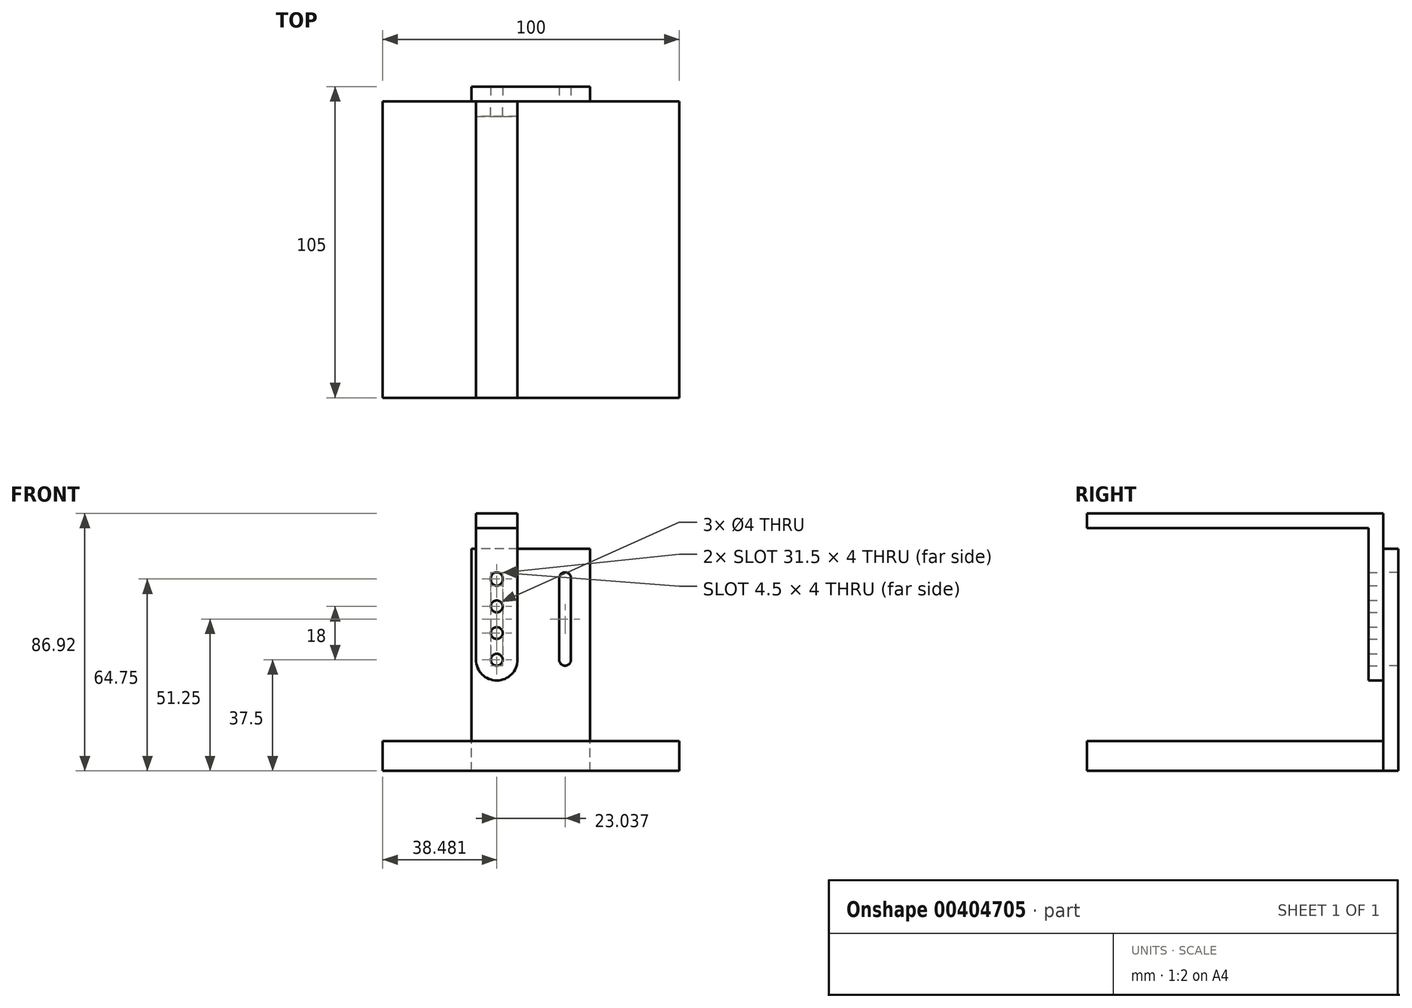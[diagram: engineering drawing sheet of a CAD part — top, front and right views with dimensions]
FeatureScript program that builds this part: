
annotation { "Feature Type Name" : "Feature", "Feature Type Description" : "" }
export const myFeature = defineFeature(function(context is Context, id is Id, definition is map)
    precondition{}
    {
        {
            assignVariable(context, id + "F0", {"name" : "zSizeBase", "anyValue" : 10});
        }
        {
            assignVariable(context, id + "F1", {"name" : "ySizeArm", "anyValue" : 5});
        }
        {
            assignVariable(context, id + "F2", {"name" : "zSizeTop", "anyValue" : 5});
        }
        {
            var Q0;
            Q0=qCreatedBy(makeId("Top.planeOp"),FACE);
            var sketch = newSketch(context, id + "F3", { "sketchPlane" : qUnion([Q0])});
            skLineSegment(sketch, "E0.bottom", {"start": v(50, -50) * mm, "end": v(-50, -50) * mm});
            skLineSegment(sketch, "E0.top", {"start": v(50, 50) * mm, "end": v(-50, 50) * mm});
            skLineSegment(sketch, "E0.left", {"start": v(50, -50) * mm, "end": v(50, 50) * mm});
            skLineSegment(sketch, "E0.right", {"start": v(-50, -50) * mm, "end": v(-50, 50) * mm});
            skPoint(sketch, "E0.middle", {"position": v(0, 0) * mm});
            skSolve(sketch);
        }
        {
            var Q0;
            Q0=makeQuery(id+"F3.imprint","IMPRINT",FACE,{"disambiguationData":[TD([[makeQuery(id+"F3.imprint","IMPRINT",EDGE,{"derivedFrom":sQuery(id+"F3.wireOp",EDGE,"E0.bottom")}),-1.0]])]});
            extrude(context, id + "F4", {"entities" : qUnion([Q0]), "depth" : (getVariable(context, 'zSizeBase')) * mm});
        }
        {
            var Q0;
            Q0=makeQuery(id+"F4.opExtrude","SWEPT_FACE",FACE,{"disambiguationData":[OSD([sQuery(id+"F3.wireOp",EDGE,"E0.top")])]});
            var sketch = newSketch(context, id + "F5", { "sketchPlane" : qUnion([Q0])});
            skLineSegment(sketch, "E1.bottom", {"start": v(-20, 0) * mm, "end": v(20, 0) * mm});
            skLineSegment(sketch, "E1.top", {"start": v(-20, 75) * mm, "end": v(20, 75) * mm});
            skLineSegment(sketch, "E1.left", {"start": v(-20, 0) * mm, "end": v(-20, 75) * mm});
            skLineSegment(sketch, "E1.right", {"start": v(20, 0) * mm, "end": v(20, 75) * mm});
            skLineSegment(sketch, "E2", {"start": v(0, 37.5) * mm, "end": v(0, 75) * mm, "construction": true});
            skLineSegment(sketch, "E3", {"start": v(0, 37.5) * mm, "end": v(0, 0) * mm, "construction": true});
            skLineSegment(sketch, "E4", {"start": v(-11.52, 75) * mm, "end": v(-11.52, 37.5) * mm, "construction": true});
            skPoint(sketch, "E4.startSnap0", {"position": v(-11.52, 37.5) * mm});
            skPoint(sketch, "E5.startSnap0", {"position": v(10, 37.5) * mm});
            skArc(sketch, "E6", {"start": v(-13.52, 65) * mm, "mid": v(-11.52, 67) * mm, "end": v(-9.52, 65) * mm});
            skLineSegment(sketch, "E7", {"start": v(-13.52, 65) * mm, "end": v(-13.52, 37.5) * mm});
            skLineSegment(sketch, "E8", {"start": v(-9.52, 65) * mm, "end": v(-9.52, 37.5) * mm});
            skArc(sketch, "E9", {"start": v(-13.52, 37.5) * mm, "mid": v(-11.52, 35.5) * mm, "end": v(-9.52, 37.5) * mm});
            skLineSegment(sketch, "E10.MirrorCS", {"start": v(9.52, 65) * mm, "end": v(9.52, 37.5) * mm});
            skArc(sketch, "E11.MirrorCS", {"start": v(13.52, 37.5) * mm, "mid": v(11.52, 35.5) * mm, "end": v(9.52, 37.5) * mm});
            skLineSegment(sketch, "E12.MirrorCS", {"start": v(13.52, 65) * mm, "end": v(13.52, 37.5) * mm});
            skArc(sketch, "E13.MirrorCS", {"start": v(13.52, 65) * mm, "mid": v(11.52, 67) * mm, "end": v(9.52, 65) * mm});
            skSolve(sketch);
        }
        {
            var Q0;
            {var subQ0=sQuery(id+"F5.wireOp",EDGE,"E1.top");Q0=makeQuery(id+"F5.imprint","IMPRINT",FACE,{"disambiguationData":[TD([[makeQuery(id+"F5.imprint","IMPRINT",EDGE,{"derivedFrom":subQ0}),-1.0]])]});}
            var Q1;
            {var subQ0=sQuery(id+"F5.wireOp",EDGE,"E1.bottom");Q1=makeQuery(id+"F5.imprint","IMPRINT",FACE,{"disambiguationData":[TD([[makeQuery(id+"F5.imprint","IMPRINT",EDGE,{"derivedFrom":subQ0}),1.0]])]});}
            extrude(context, id + "F6", {"entities" : qUnion([Q0, Q1]), "operationType" : NewBodyOperationType.ADD, "depth" : (getVariable(context, 'ySizeArm')) * mm});
        }
        {
            var Q0;
            {var subQ0=sQuery(id+"F5.wireOp",EDGE,"E1.top");Q0=makeQuery(id+"F5.imprint","IMPRINT",FACE,{"disambiguationData":[TD([[makeQuery(id+"F5.imprint","IMPRINT",EDGE,{"derivedFrom":subQ0}),-1.0]])]});}
            var sketch = newSketch(context, id + "F7", { "sketchPlane" : qUnion([Q0])});
            skPoint(sketch, "E14.0", {"position": v(11.52, 37.5) * mm});
            skPoint(sketch, "E15.0", {"position": v(9.52, 37.5) * mm});
            skArc(sketch, "E16", {"start": v(4.52, 37.5) * mm, "mid": v(11.52, 30.5) * mm, "end": v(18.52, 37.5) * mm});
            skPoint(sketch, "E17.0", {"position": v(0, 75) * mm});
            skLineSegment(sketch, "E18", {"start": v(4.52, 37.5) * mm, "end": v(4.52, 81.92) * mm});
            skLineSegment(sketch, "E19", {"start": v(4.52, 81.92) * mm, "end": v(18.52, 81.92) * mm});
            skLineSegment(sketch, "E20", {"start": v(18.52, 81.92) * mm, "end": v(18.52, 37.5) * mm});
            skLineSegment(sketch, "E21", {"start": v(18.52, 37.5) * mm, "end": v(11.52, 37.5) * mm, "construction": true});
            skLineSegment(sketch, "E22", {"start": v(11.52, 37.5) * mm, "end": v(4.52, 37.5) * mm, "construction": true});
            skLineSegment(sketch, "E23", {"start": v(18.52, 81.92) * mm, "end": v(18.52, 86.92) * mm});
            skLineSegment(sketch, "E24", {"start": v(18.52, 86.92) * mm, "end": v(4.52, 86.92) * mm});
            skLineSegment(sketch, "E25", {"start": v(4.52, 86.92) * mm, "end": v(4.52, 81.92) * mm});
            skPoint(sketch, "E26.0", {"position": v(11.52, 65) * mm});
            skCircle(sketch, "E27", {"center": v(11.52, 37.5) * mm, "radius": 2 * mm});
            skCircle(sketch, "E28.0.1.0", {"center": v(11.52, 46.5) * mm, "radius": 2 * mm});
            skCircle(sketch, "E28.0.2.0", {"center": v(11.52, 55.5) * mm, "radius": 2 * mm});
            skCircle(sketch, "E28.0.3.0", {"center": v(11.52, 64.5) * mm, "radius": 2 * mm});
            skLineSegment(sketch, "E28.direction1", {"start": v(11.52, 37.5) * mm, "end": v(36.52, 37.5) * mm, "construction": true});
            skLineSegment(sketch, "E28.direction2", {"start": v(11.52, 37.5) * mm, "end": v(11.52, 46.5) * mm, "construction": true});
            skSolve(sketch);
        }
        {
            var Q0;
            Q0=makeQuery(id+"F7.imprint","IMPRINT",FACE,{"disambiguationData":[TD([[makeQuery(id+"F7.imprint","IMPRINT",EDGE,{"derivedFrom":sQuery(id+"F7.wireOp",EDGE,"E19")}),1.0]])]});
            var Q1;
            {var subQ0=sQuery(id+"F7.wireOp",EDGE,"E19");Q1=makeQuery(id+"F7.imprint","IMPRINT",FACE,{"disambiguationData":[TD([[makeQuery(id+"F7.imprint","IMPRINT",EDGE,{"derivedFrom":subQ0}),-1.0]])]});}
            var Q2;
            {var subQ0=sQuery(id+"F7.wireOp",EDGE,"E28.0.1.0");var subQ1=makeQuery(id+"F5.imprint","IMPRINT",EDGE,{"derivedFrom":sQuery(id+"F5.wireOp",EDGE,"E10.MirrorCS")});var subQ2=makeQuery(id+"F7.imprint","INTERSECT",VERTEX,{"derivedFrom":[subQ1,subQ0]});Q2=makeQuery(id+"F7.imprint","IMPRINT",FACE,{"disambiguationData":[TD([[makeQuery(id+"F7.imprint","IMPRINT",EDGE,{"disambiguationData":[TD([[subQ2,1.0]])],"derivedFrom":subQ0}),-1.0]])]});}
            var Q3;
            {var subQ0=sQuery(id+"F7.wireOp",EDGE,"E28.0.2.0");var subQ1=makeQuery(id+"F5.imprint","IMPRINT",EDGE,{"derivedFrom":sQuery(id+"F5.wireOp",EDGE,"E10.MirrorCS")});var subQ2=makeQuery(id+"F7.imprint","INTERSECT",VERTEX,{"derivedFrom":[subQ1,subQ0]});Q3=makeQuery(id+"F7.imprint","IMPRINT",FACE,{"disambiguationData":[TD([[makeQuery(id+"F7.imprint","IMPRINT",EDGE,{"disambiguationData":[TD([[subQ2,1.0]])],"derivedFrom":subQ0}),-1.0]])]});}
            var Q4;
            {var subQ0=sQuery(id+"F7.wireOp",EDGE,"E27");Q4=makeQuery(id+"F7.imprint","IMPRINT",FACE,{"disambiguationData":[TD([[makeQuery(id+"F7.imprint","IMPRINT",EDGE,{"disambiguationData":[OD(0.0)],"derivedFrom":subQ0}),-1.0]])]});}
            var Q5;
            {var subQ11=sQuery(id+"F7.wireOp",EDGE,"E16");Q5=makeQuery(id+"F7.imprint","IMPRINT",FACE,{"disambiguationData":[TD([[makeQuery(id+"F7.imprint","IMPRINT",EDGE,{"derivedFrom":subQ11}),1.0]])]});}
            extrude(context, id + "F8", {"entities" : qUnion([Q0, Q1, Q2, Q3, Q4, Q5]), "oppositeDirection" : true, "depth" : (getVariable(context, 'ySizeArm')) * mm});
        }
        {
            var Q0;
            Q0=makeQuery(id+"F8.opExtrude","SWEPT_FACE",FACE,{"disambiguationData":[OSD([sQuery(id+"F7.wireOp",EDGE,"E24")])]});
            var sketch = newSketch(context, id + "F9", { "sketchPlane" : qUnion([Q0])});
            skPoint(sketch, "E29.0", {"position": v(-18.52, 45) * mm});
            skPoint(sketch, "E30.0", {"position": v(-4.52, 45) * mm});
            skPoint(sketch, "E31.0", {"position": v(-50, -50) * mm});
            skPoint(sketch, "E32.0", {"position": v(50, -50) * mm});
            skPoint(sketch, "E33.0", {"position": v(50, 50) * mm});
            skPoint(sketch, "E34.0", {"position": v(-50, 50) * mm});
            skLineSegment(sketch, "E35", {"start": v(-18.52, 45) * mm, "end": v(-18.52, -50) * mm});
            skLineSegment(sketch, "E36", {"start": v(-18.52, -50) * mm, "end": v(-4.52, -50) * mm});
            skLineSegment(sketch, "E37", {"start": v(-4.52, -50) * mm, "end": v(-4.52, 45) * mm});
            skSolve(sketch);
        }
        {
            var Q0;
            Q0=makeQuery(id+"F9.imprint","IMPRINT",FACE,{"disambiguationData":[TD([[makeQuery(id+"F9.imprint","IMPRINT",EDGE,{"derivedFrom":sQuery(id+"F9.wireOp",EDGE,"E35")}),1.0]])]});
            extrude(context, id + "F10", {"entities" : qUnion([Q0]), "operationType" : NewBodyOperationType.ADD, "oppositeDirection" : true, "depth" : (getVariable(context, 'zSizeTop')) * mm});
        }
    });
